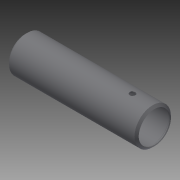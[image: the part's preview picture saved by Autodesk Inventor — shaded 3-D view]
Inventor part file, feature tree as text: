
AUTODESK INVENTOR PART (.ipt)
format: ipt  version: 2014 (Build 180170000, 170)  size: 140,288 bytes
history: native  units: in
note: dims shown in document units (in); Inventor stores cm internally (conversion verified against a paired STEP export)
features: other x56, revolve x2, sketch x2
ambient origin geometry x8: Origin, YZ Plane, XZ Plane, XY Plane, X Axis, Y Axis, Z Axis, Center Point
bodies: Solid1 (feature_tree)
feature tree (60):
  revolve  "Revolution1"  Angle=360.0deg
  revolve  "Revolution2"  [1 undecoded]
  other  "o1_XY"
  other  "o1_YZ"
  other  "o1_ZX"
  other  "o1_X"
  other  "o1_Y"
  other  "o1_Z"
  other  "o1_Center"
  other  "o2_XY"
  other  "o2_YZ"
  other  "o2_ZX"
  other  "o2_X"
  other  "o2_Y"
  other  "o2_Z"
  other  "o2_Center"
  other  "t1_XY"
  other  "t1_YZ"
  other  "t1_ZX"
  other  "t1_X"
  other  "t1_Y"
  other  "t1_Z"
  other  "t1_Center"
  other  "t2_XY"
  other  "t2_YZ"
  other  "t2_ZX"
  other  "t2_X"
  other  "t2_Y"
  other  "t2_Z"
  other  "t2_Center"
  other  "t3_XY"
  other  "t3_YZ"
  other  "t3_ZX"
  other  "t3_X"
  other  "t3_Y"
  other  "t3_Z"
  other  "t3_Center"
  other  "t4_XY"
  other  "t4_YZ"
  other  "t4_ZX"
  other  "t4_X"
  other  "t4_Y"
  other  "t4_Z"
  other  "t4_Center"
  other  "tube1_XY"
  other  "tube1_YZ"
  other  "tube1_ZX"
  other  "tube1_X"
  other  "tube1_Y"
  other  "tube1_Z"
  other  "tube1_Center"
  other  "tube2_XY"
  other  "tube2_YZ"
  other  "tube2_ZX"
  other  "tube2_X"
  other  "tube2_Y"
  other  "tube2_Z"
  other  "tube2_Center"
  sketch  "Sketch_5"
  sketch  "Sketch_1"  dims[d0=360.0deg d1=360.0deg]
note: 1 required parameter value undecoded (feature->parameter linkage not recoverable at this tier; creation-order binding heuristic only, values carry confidence <= 0.55)
